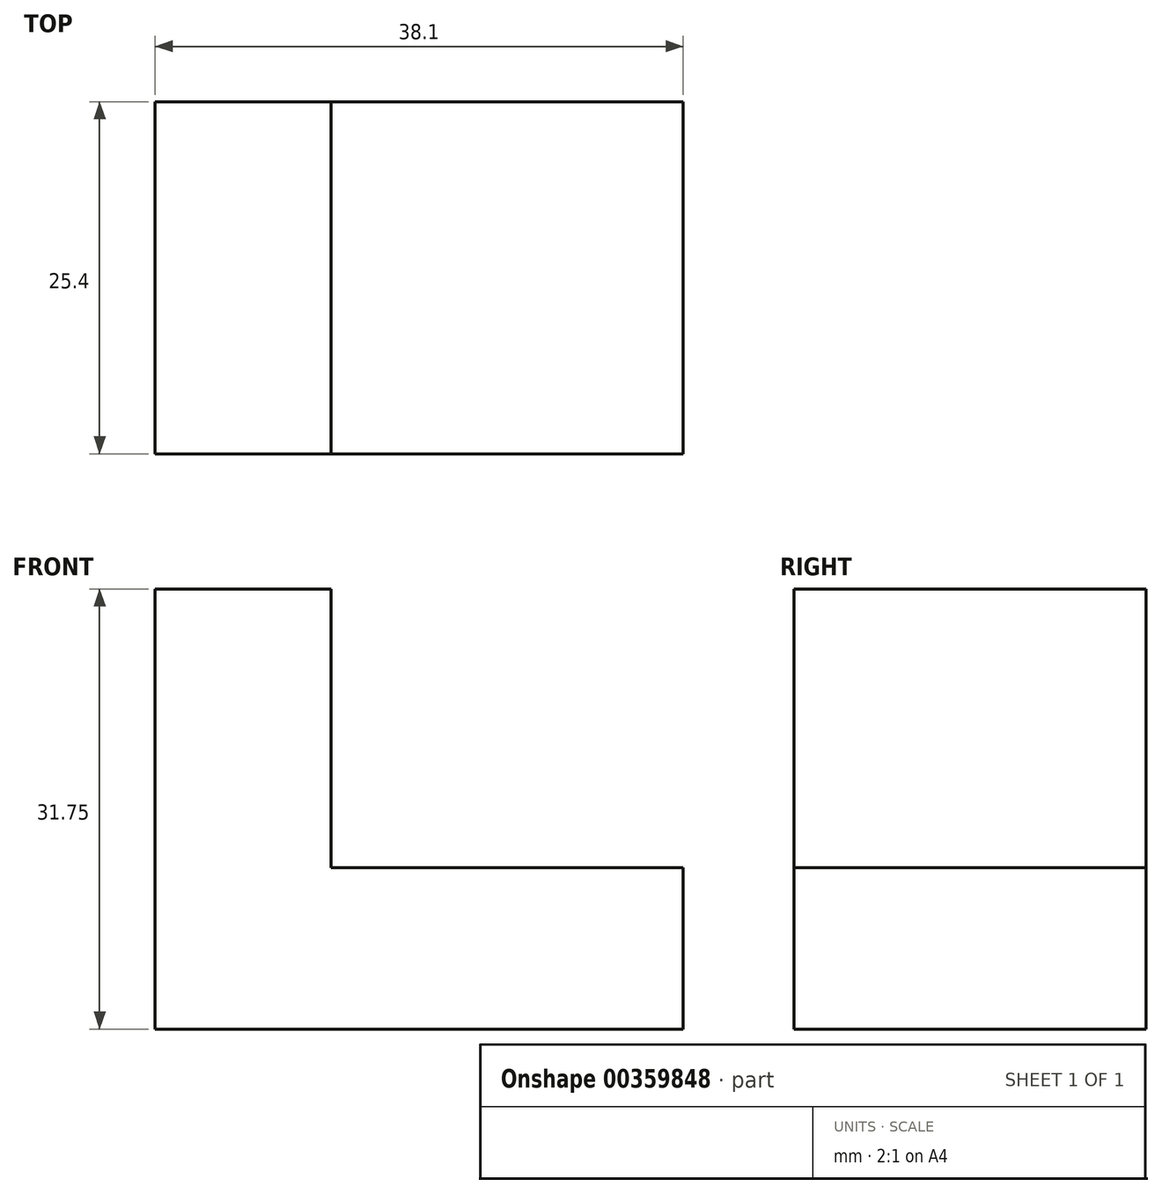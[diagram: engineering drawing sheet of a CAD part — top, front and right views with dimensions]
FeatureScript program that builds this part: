
annotation { "Feature Type Name" : "Feature", "Feature Type Description" : "" }
export const myFeature = defineFeature(function(context is Context, id is Id, definition is map)
    precondition{}
    {
        {
            var Q0;
            Q0=qCreatedBy(makeId("Front.planeOp"),FACE);
            var sketch = newSketch(context, id + "F0", { "sketchPlane" : qUnion([Q0])});
            skLineSegment(sketch, "E0", {"start": v(0, 0) * mm, "end": v(0, 31.75) * mm});
            skLineSegment(sketch, "E1", {"start": v(0, 31.75) * mm, "end": v(12.7, 31.75) * mm});
            skLineSegment(sketch, "E2", {"start": v(12.7, 31.75) * mm, "end": v(12.7, 11.63) * mm});
            skLineSegment(sketch, "E3", {"start": v(12.7, 11.63) * mm, "end": v(38.1, 11.63) * mm});
            skLineSegment(sketch, "E4", {"start": v(38.1, 11.63) * mm, "end": v(38.1, 0) * mm});
            skLineSegment(sketch, "E5", {"start": v(38.1, 0) * mm, "end": v(0, 0) * mm});
            skSolve(sketch);
        }
        {
            var Q0;
            Q0 = qSketchRegion(id + "F0", true);
            extrude(context, id + "F1", {"entities" : qUnion([Q0]), "depth" : 25.4 * mm});
        }
    });
